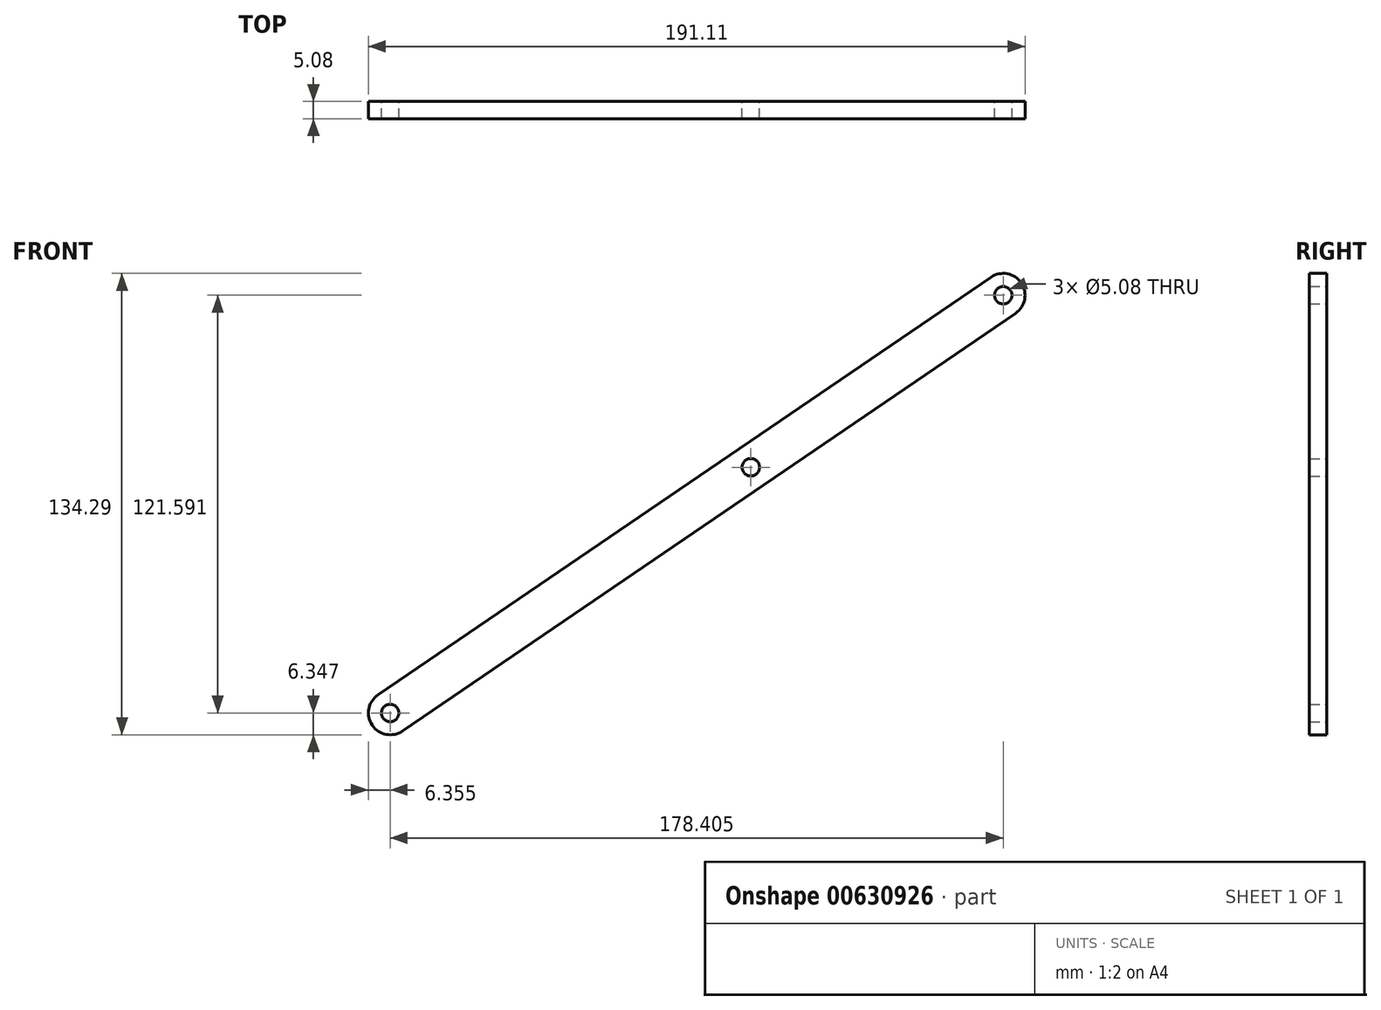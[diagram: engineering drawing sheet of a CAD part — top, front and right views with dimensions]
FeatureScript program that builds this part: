
annotation { "Feature Type Name" : "Feature", "Feature Type Description" : "" }
export const myFeature = defineFeature(function(context is Context, id is Id, definition is map)
    precondition{}
    {
        {
            var Q0;
            Q0=qCreatedBy(makeId("Front.planeOp"),FACE);
            var sketch = newSketch(context, id + "F0", { "sketchPlane" : qUnion([Q0])});
            skCircle(sketch, "E0", {"center": v(-45.83, -5.37) * mm, "radius": 6.35 * mm});
            skCircle(sketch, "E1", {"center": v(-45.83, -5.37) * mm, "radius": 2.54 * mm});
            skCircle(sketch, "E2", {"center": v(59.12, 66.15) * mm, "radius": 6.35 * mm});
            skCircle(sketch, "E3", {"center": v(59.12, 66.15) * mm, "radius": 2.54 * mm});
            skCircle(sketch, "E4", {"center": v(132.58, 116.22) * mm, "radius": 6.35 * mm});
            skCircle(sketch, "E5", {"center": v(132.58, 116.22) * mm, "radius": 2.54 * mm});
            skLineSegment(sketch, "E6", {"start": v(-49.4, -0.13) * mm, "end": v(129, 121.47) * mm});
            skLineSegment(sketch, "E7", {"start": v(-42.25, -10.62) * mm, "end": v(136.16, 110.97) * mm});
            skSolve(sketch);
        }
        {
            var Q0;
            Q0 = qSketchRegion(id + "F0", true);
            extrude(context, id + "F1", {"entities" : qUnion([Q0]), "depth" : 5.08 * mm, "offsetDistance" : 25.4 * mm});
        }
    });
